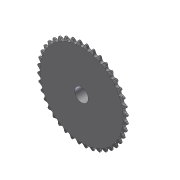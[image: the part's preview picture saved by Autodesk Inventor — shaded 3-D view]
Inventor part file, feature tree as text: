
AUTODESK INVENTOR PART (.ipt)
format: ipt  version: 2012 (Build 160160000, 160)  size: 910,336 bytes
history: native  units: in
note: dims shown in document units (in); Inventor stores cm internally (conversion verified against a paired STEP export)
features: other x2, extrude x1, chamfer x1, imported_body x1, sketch x1
ambient origin geometry x8: Origin, YZ Plane, XZ Plane, XY Plane, X Axis, Y Axis, Z Axis, Center Point
feature tree (6):
  parser-record x1  (decoder bookkeeping rows leaked as tree rows — omitted from the tree; the rows remain in map.json)
  other  "2737T2811"
  extrude  "Extrusion2"  Depth=0.375in TaperAngle=45.0deg
  chamfer  "Chamfer2"  [1 undecoded]
  imported_body  "Base1"
  sketch  "Sketch2"  dims[d5=0.125in d6=0.0in d7=0.375in d8=0.125in d9=45.0deg]
note: 1 required parameter value undecoded (feature->parameter linkage not recoverable at this tier; creation-order binding heuristic only, values carry confidence <= 0.55)
